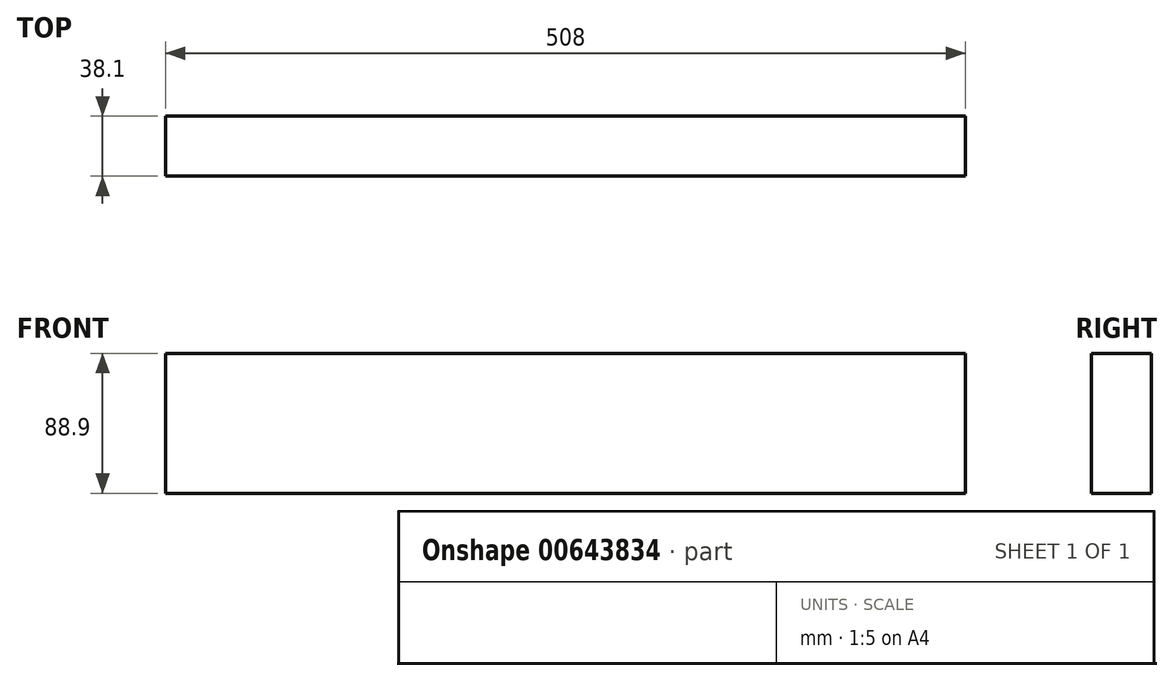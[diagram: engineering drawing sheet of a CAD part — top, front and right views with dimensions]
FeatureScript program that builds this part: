
annotation { "Feature Type Name" : "Feature", "Feature Type Description" : "" }
export const myFeature = defineFeature(function(context is Context, id is Id, definition is map)
    precondition{}
    {
        {
            var Q0;
            Q0=qCreatedBy(makeId("Front.planeOp"),FACE);
            var sketch = newSketch(context, id + "F0", { "sketchPlane" : qUnion([Q0])});
            skLineSegment(sketch, "E0.bottom", {"start": v(254, -44.45) * mm, "end": v(-254, -44.45) * mm});
            skLineSegment(sketch, "E0.top", {"start": v(254, 44.45) * mm, "end": v(-254, 44.45) * mm});
            skLineSegment(sketch, "E0.left", {"start": v(254, -44.45) * mm, "end": v(254, 44.45) * mm});
            skLineSegment(sketch, "E0.right", {"start": v(-254, -44.45) * mm, "end": v(-254, 44.45) * mm});
            skPoint(sketch, "E0.middle", {"position": v(0, 0) * mm});
            skSolve(sketch);
        }
        {
            var Q0;
            Q0=qSketchRegion(id+"F0",true);
            extrude(context, id + "F1", {"entities" : qUnion([Q0]), "depth" : 38.1 * mm, "offsetDistance" : 25.4 * mm});
        }
    });
